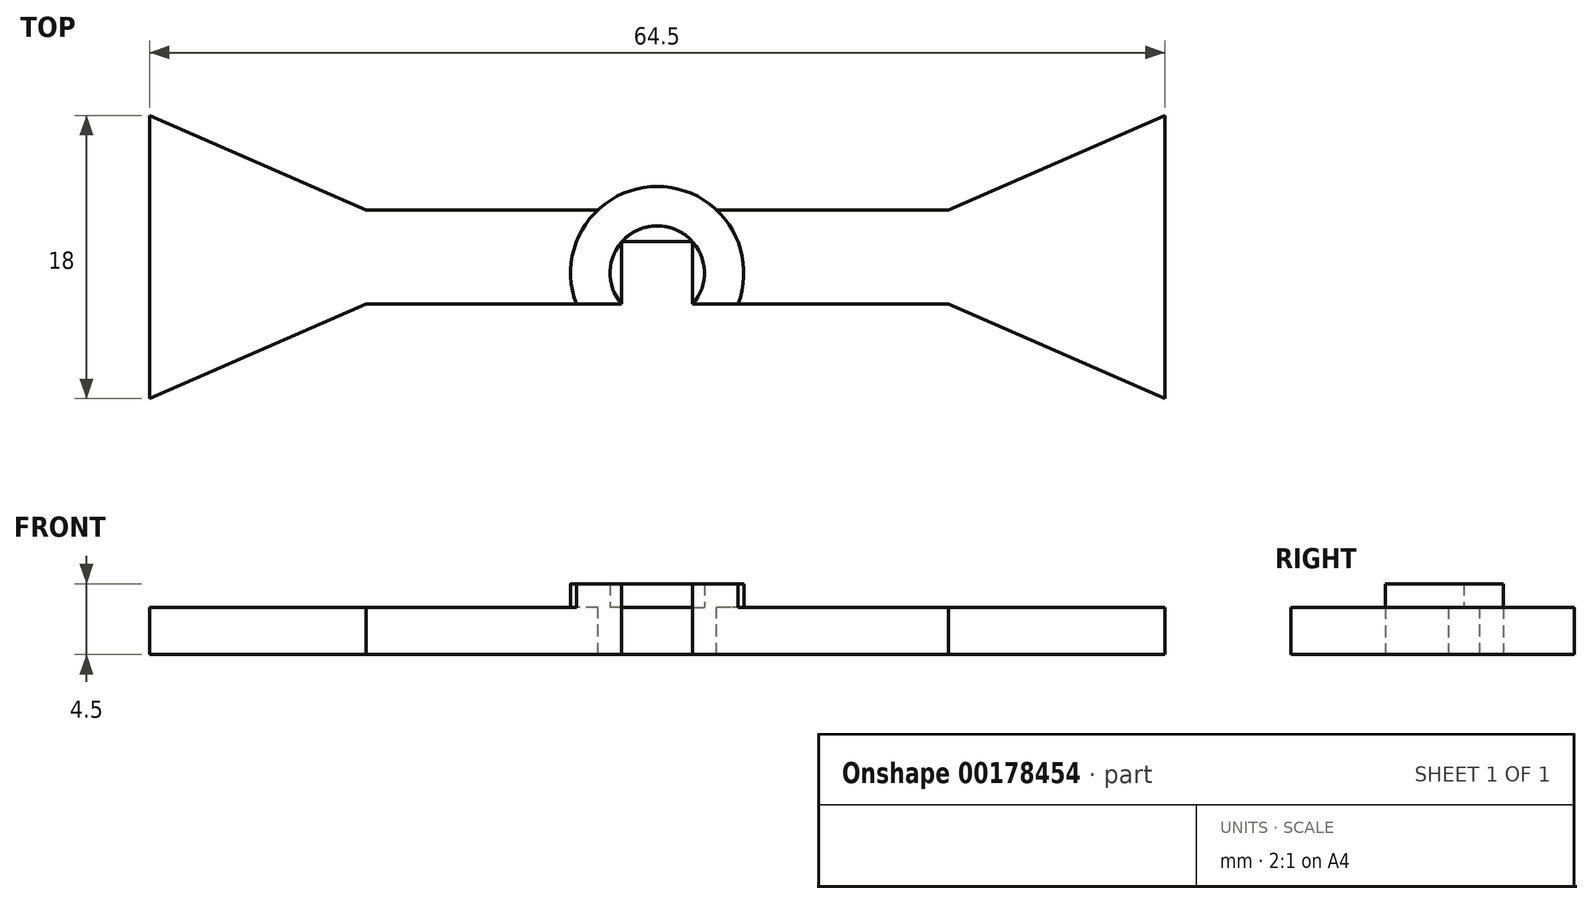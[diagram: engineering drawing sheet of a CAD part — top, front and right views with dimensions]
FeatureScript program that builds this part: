
annotation { "Feature Type Name" : "Feature", "Feature Type Description" : "" }
export const myFeature = defineFeature(function(context is Context, id is Id, definition is map)
    precondition{}
    {
        {
            var Q0;
            Q0=qCreatedBy(makeId("Top.planeOp"),FACE);
            var sketch = newSketch(context, id + "F0", { "sketchPlane" : qUnion([Q0])});
            skLineSegment(sketch, "E0.bottom", {"start": v(0, 0) * mm, "end": v(30, 0) * mm});
            skLineSegment(sketch, "E0.top", {"start": v(0, 6) * mm, "end": v(30, 6) * mm});
            skLineSegment(sketch, "E0.left", {"start": v(0, 0) * mm, "end": v(0, 6) * mm});
            skLineSegment(sketch, "E0.right", {"start": v(30, 0) * mm, "end": v(30, 6) * mm});
            skLineSegment(sketch, "E1.bottom", {"start": v(0, 6) * mm, "end": v(-4.5, 6) * mm});
            skLineSegment(sketch, "E1.top", {"start": v(0, 4) * mm, "end": v(-4.5, 4) * mm});
            skLineSegment(sketch, "E1.left", {"start": v(0, 6) * mm, "end": v(0, 4) * mm});
            skLineSegment(sketch, "E1.right", {"start": v(-4.5, 6) * mm, "end": v(-4.5, 4) * mm});
            skLineSegment(sketch, "E2.bottom", {"start": v(-4.5, 6) * mm, "end": v(-34.5, 6) * mm});
            skLineSegment(sketch, "E2.top", {"start": v(-4.5, 0) * mm, "end": v(-34.5, 0) * mm});
            skLineSegment(sketch, "E2.left", {"start": v(-4.5, 6) * mm, "end": v(-4.5, 0) * mm});
            skLineSegment(sketch, "E2.right", {"start": v(-34.5, 6) * mm, "end": v(-34.5, 0) * mm});
            skLineSegment(sketch, "E3", {"start": v(30, 0) * mm, "end": v(30, -6) * mm});
            skLineSegment(sketch, "E4", {"start": v(30, -6) * mm, "end": v(16.25, 0) * mm});
            skLineSegment(sketch, "E5", {"start": v(30, 6) * mm, "end": v(30, 12) * mm});
            skLineSegment(sketch, "E6", {"start": v(30, 12) * mm, "end": v(16.25, 6) * mm});
            skLineSegment(sketch, "E7", {"start": v(-34.5, 6) * mm, "end": v(-34.5, 12) * mm});
            skLineSegment(sketch, "E8", {"start": v(-34.5, 12) * mm, "end": v(-20.75, 6) * mm});
            skLineSegment(sketch, "E9", {"start": v(-34.5, 0) * mm, "end": v(-34.5, -6) * mm});
            skLineSegment(sketch, "E10", {"start": v(-34.5, -6) * mm, "end": v(-20.75, 0) * mm});
            skSolve(sketch);
        }
        {
            var Q0;
            Q0 = qSketchRegion(id + "F0", true);
            extrude(context, id + "F1", {"entities" : qUnion([Q0]), "depth" : 3 * mm});
        }
        {
            var Q0;
            Q0=makeQuery(id+"F1.opExtrude","CAP_FACE",FACE,{"disambiguationData":[OSD([sQuery(id+"F0.wireOp",EDGE,"E0.bottom"),sQuery(id+"F0.wireOp",EDGE,"E0.top"),sQuery(id+"F0.wireOp",EDGE,"E0.left"),sQuery(id+"F0.wireOp",EDGE,"E0.right"),sQuery(id+"F0.wireOp",EDGE,"E1.bottom"),sQuery(id+"F0.wireOp",EDGE,"E1.top"),sQuery(id+"F0.wireOp",EDGE,"E2.bottom"),sQuery(id+"F0.wireOp",EDGE,"E2.top"),sQuery(id+"F0.wireOp",EDGE,"E2.left"),sQuery(id+"F0.wireOp",EDGE,"E2.right"),sQuery(id+"F0.wireOp",EDGE,"E3"),sQuery(id+"F0.wireOp",EDGE,"E4"),sQuery(id+"F0.wireOp",EDGE,"E5"),sQuery(id+"F0.wireOp",EDGE,"E6"),sQuery(id+"F0.wireOp",EDGE,"E7"),sQuery(id+"F0.wireOp",EDGE,"E8"),sQuery(id+"F0.wireOp",EDGE,"E9"),sQuery(id+"F0.wireOp",EDGE,"E10")])],"isStart":false});
            var sketch = newSketch(context, id + "F2", { "sketchPlane" : qUnion([Q0])});
            skPoint(sketch, "E11", {"position": v(-2.25, 1.98) * mm});
            skArc(sketch, "E12", {"start": v(0, 0) * mm, "mid": v(-2.25, 4.98) * mm, "end": v(-4.5, 0) * mm});
            skArc(sketch, "E13", {"start": v(2.88, 0) * mm, "mid": v(-2.25, 7.48) * mm, "end": v(-7.38, 0) * mm});
            skLineSegment(sketch, "E14", {"start": v(0, 0) * mm, "end": v(2.88, 0) * mm});
            skLineSegment(sketch, "E15", {"start": v(-7.38, 0) * mm, "end": v(-4.5, 0) * mm});
            skSolve(sketch);
        }
        {
            var Q0;
            Q0 = qSketchRegion(id + "F2", true);
            extrude(context, id + "F3", {"entities" : qUnion([Q0]), "operationType" : NewBodyOperationType.ADD, "depth" : 1.5 * mm});
        }
        {
            var Q0;
            {var subQ0=sQuery(id+"F0.wireOp",EDGE,"E2.left");var subQ4=sQuery(id+"F0.wireOp",EDGE,"E0.left");var subQ8=sQuery(id+"F2.wireOp",EDGE,"E12");var subQ10=sQuery(id+"F2.wireOp",EDGE,"E13");var subQ11=makeQuery(id+"F3.opExtrude","CAP_FACE",FACE,{"disambiguationData":[OSD([subQ8,subQ10,sQuery(id+"F2.wireOp",EDGE,"E14"),sQuery(id+"F2.wireOp",EDGE,"E15")])],"isStart":true});Q0=qUnion([makeQuery(id+"F3.boolean.opBoolean","SPLIT",FACE,{"disambiguationData":[TD([makeQuery(id+"F3.opExtrude","SWEPT_FACE",FACE,{"disambiguationData":[OSD([subQ10])]})])],"derivedFrom":subQ11}),makeQuery(id+"F3.boolean.opBoolean","SPLIT",FACE,{"disambiguationData":[TD([makeQuery(id+"F1.opExtrude","SWEPT_FACE",FACE,{"disambiguationData":[OSD([subQ4])]})])],"derivedFrom":subQ11}),makeQuery(id+"F3.boolean.opBoolean","SPLIT",FACE,{"disambiguationData":[TD([makeQuery(id+"F1.opExtrude","SWEPT_FACE",FACE,{"disambiguationData":[OSD([subQ0])]})])],"derivedFrom":subQ11})]);}
            var sketch = newSketch(context, id + "F4", { "sketchPlane" : qUnion([Q0])});
            skLineSegment(sketch, "E16", {"start": v(1.5, -6) * mm, "end": v(-6, -6) * mm});
            skArc(sketch, "E17.0", {"start": v(1.5, -6) * mm, "mid": v(-2.25, -7.48) * mm, "end": v(-6, -6) * mm});
            skSolve(sketch);
        }
        {
            var Q0;
            Q0 = qSketchRegion(id + "F4", true);
            extrude(context, id + "F5", {"entities" : qUnion([Q0]), "operationType" : NewBodyOperationType.ADD, "depth" : 3 * mm});
        }
    });
